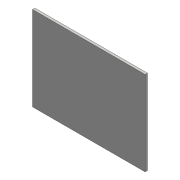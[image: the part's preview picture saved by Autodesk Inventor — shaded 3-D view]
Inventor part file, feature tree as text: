
AUTODESK INVENTOR PART (.ipt)
format: ipt  version: 2016 (Build 200138000, 138)  size: 66,048 bytes
history: native  units: mm
features: extrude x1, sketch x1
ambient origin geometry x8: Origin, YZ Plane, XZ Plane, XY Plane, X Axis, Y Axis, Z Axis, Center Point
bodies: Solid1 (feature_tree)
feature tree (2):
  extrude  "Extrusion1"  Depth=304.8mm
  sketch  "Sketch1"  dims[d0=228.6mm d1=304.8mm d2=6.35mm d3=0.0mm]
